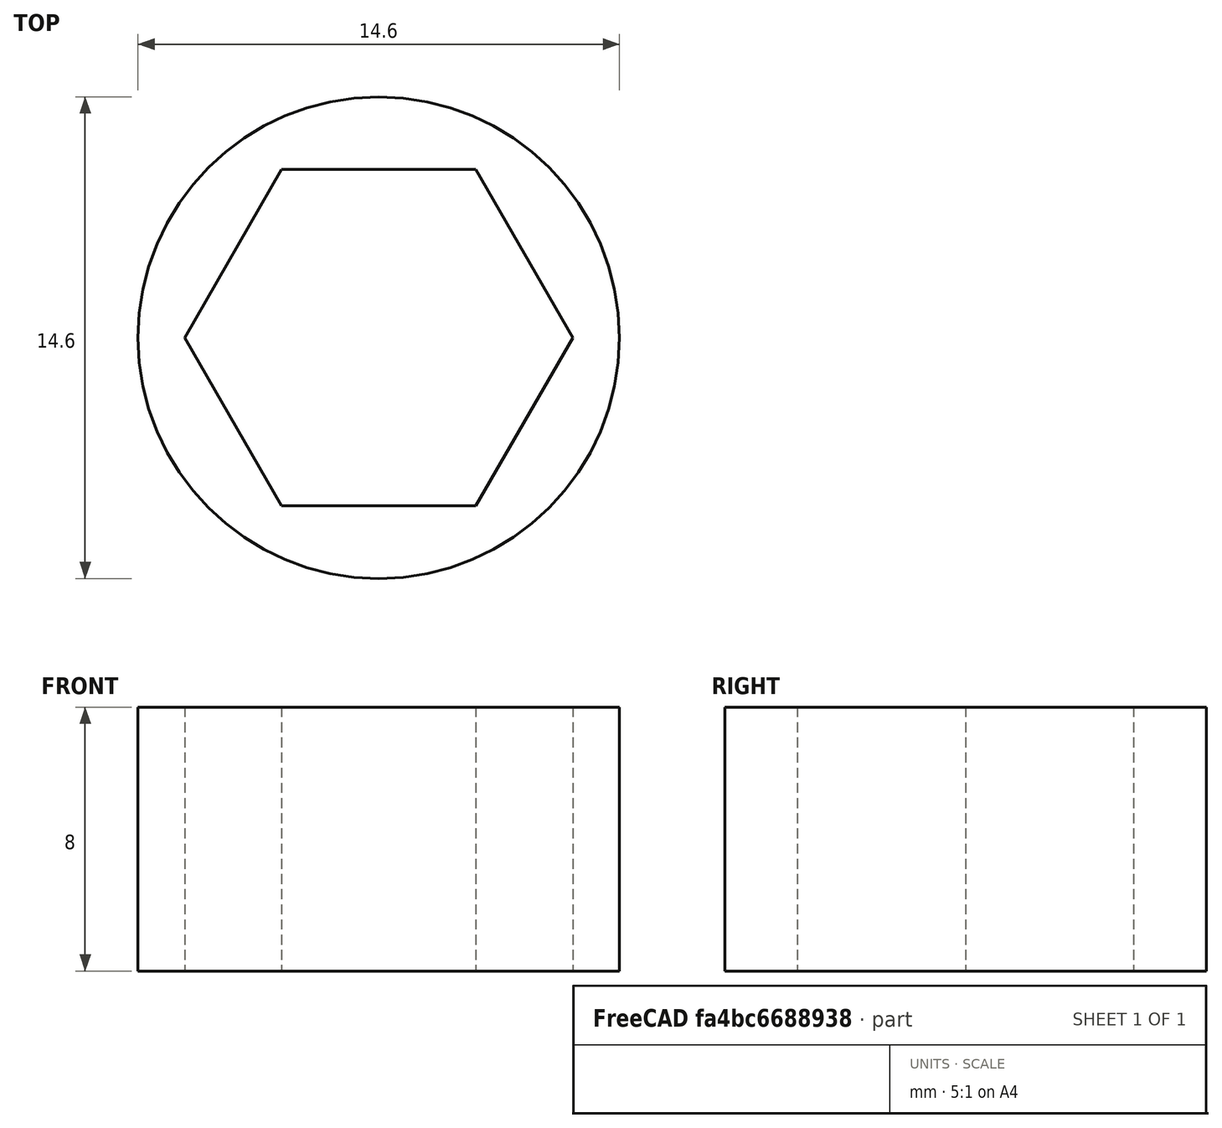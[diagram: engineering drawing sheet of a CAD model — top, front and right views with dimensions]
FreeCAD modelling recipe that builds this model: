
FCSTD DOCUMENT  (FreeCAD 0.16R6706 (Git))
Label: DriveLinkV2B-15mm
License: All rights reserved
LicenseURL: http://en.wikipedia.org/wiki/All_rights_reserved
objects: Sketcher::SketchObject×1, PartDesign::Pad×1
note: 3 computed .brp shape members not serialized (recipe doc carries the construction recipe); baked Part::Feature solids carry a one-line shape summary decoded from their .brp

FEATURE [Sketcher::SketchObject] Sketch002
  Placement = pos=(0,0,0) rot=(1,0,0;3.14159rad)
  sketch-geometry (8):
    g0: Circle CenterX=-32 CenterY=0 CenterZ=0 NormalX=0 NormalY=0 NormalZ=1 Radius=7.3
    g1: LineSegment StartX=-34.9445 StartY=5.1 StartZ=0 EndX=-37.889 EndY=0 EndZ=0
    g2: LineSegment StartX=-37.889 StartY=0 StartZ=0 EndX=-34.9445 EndY=-5.1 EndZ=0
    g3: LineSegment StartX=-34.9445 StartY=-5.1 StartZ=0 EndX=-29.0555 EndY=-5.1 EndZ=0
    g4: LineSegment StartX=-29.0555 StartY=-5.1 StartZ=0 EndX=-26.111 EndY=0 EndZ=0
    g5: LineSegment StartX=-26.111 StartY=0 StartZ=0 EndX=-29.0555 EndY=5.1 EndZ=0
    g6: LineSegment StartX=-29.0555 StartY=5.1 StartZ=0 EndX=-34.9445 EndY=5.1 EndZ=0
    g7: Circle [constr] CenterX=-32 CenterY=0 CenterZ=0 NormalX=0 NormalY=0 NormalZ=1 Radius=5.88897
  constraints (19):
    c: PointOnObject(g0,g-1)
    c: DistanceX(g0,g-1) = 32
    c: Radius(g0) = 7.3
    c: Coincident(g1,g2)
    c: Coincident(g2,g3)
    c: Coincident(g3,g4)
    c: Coincident(g4,g5)
    c: Coincident(g5,g6)
    c: Coincident(g6,g1)
    c: Equal(g1, g2-g6) x5
    c: PointOnObject(g1,g7)
    c: PointOnObject(g2,g7)
    c: PointOnObject(g3,g7)
    c: PointOnObject(g4,g7)
    c: PointOnObject(g5,g7)
    c: PointOnObject(g6,g7)
    c: Coincident(g7,g0)
    c: Horizontal(g3)
    c: DistanceY(g3,g5) = 10.2
FEATURE [PartDesign::Pad] Pad
  Length = 8
  Length2 = 100
  Placement = pos=(0,0,0) rot=(1,0,0;3.14159rad)
  Sketch = -> Sketch002
  Type = 0
